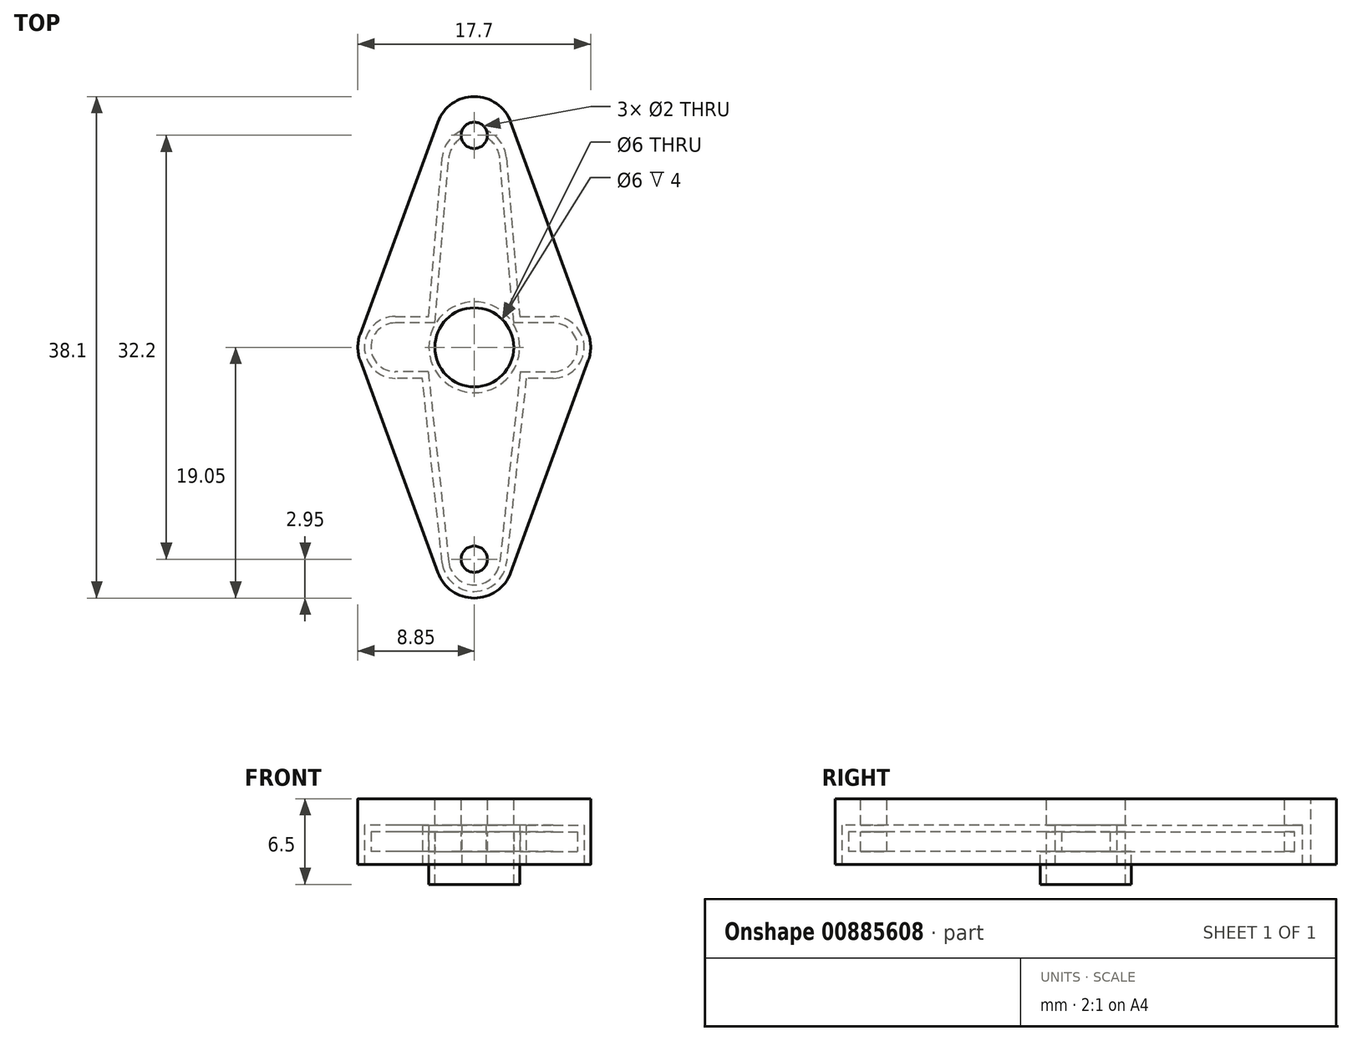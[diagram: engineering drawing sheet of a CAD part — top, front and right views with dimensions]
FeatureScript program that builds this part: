
annotation { "Feature Type Name" : "Feature", "Feature Type Description" : "" }
export const myFeature = defineFeature(function(context is Context, id is Id, definition is map)
    precondition{}
    {
        {
            var Q0;
            Q0=qCreatedBy(makeId("Top.planeOp"),FACE);
            var sketch = newSketch(context, id + "F0", { "sketchPlane" : qUnion([Q0])});
            skLineSegment(sketch, "E0.bottom", {"start": v(3.5, 1.85) * mm, "end": v(-3.5, 1.85) * mm});
            skLineSegment(sketch, "E0.top", {"start": v(3.5, -1.85) * mm, "end": v(-3.5, -1.85) * mm});
            skLineSegment(sketch, "E0.left", {"start": v(3.5, 1.85) * mm, "end": v(3.5, -1.85) * mm});
            skLineSegment(sketch, "E0.right", {"start": v(-3.5, 1.85) * mm, "end": v(-3.5, -1.85) * mm});
            skPoint(sketch, "E0.middle", {"position": v(0, 0) * mm});
            skLineSegment(sketch, "E1", {"start": v(0, 0) * mm, "end": v(0, 14.2) * mm});
            skCircle(sketch, "E2", {"center": v(0, 14.2) * mm, "radius": 1.95 * mm});
            skLineSegment(sketch, "E3", {"start": v(0, 0) * mm, "end": v(0, -16.1) * mm});
            skCircle(sketch, "E4", {"center": v(0, -16.1) * mm, "radius": 1.95 * mm});
            skLineSegment(sketch, "E5", {"start": v(0, 0) * mm, "end": v(-6, 0) * mm});
            skLineSegment(sketch, "E6", {"start": v(0, 0) * mm, "end": v(6, 0) * mm});
            skCircle(sketch, "E7", {"center": v(6, 0) * mm, "radius": 1.85 * mm});
            skCircle(sketch, "E8", {"center": v(-6, 0) * mm, "radius": 1.85 * mm});
            skLineSegment(sketch, "E9", {"start": v(3.5, 1.85) * mm, "end": v(6, 1.85) * mm});
            skLineSegment(sketch, "E10", {"start": v(3.5, -1.85) * mm, "end": v(6, -1.85) * mm});
            skLineSegment(sketch, "E11", {"start": v(-3.5, 1.85) * mm, "end": v(-6, 1.85) * mm});
            skLineSegment(sketch, "E12", {"start": v(-3.5, -1.85) * mm, "end": v(-6, -1.85) * mm});
            skLineSegment(sketch, "E13", {"start": v(3.5, -1.85) * mm, "end": v(1.94, -16.3) * mm});
            skLineSegment(sketch, "E14", {"start": v(-3.5, -1.85) * mm, "end": v(-1.94, -16.3) * mm});
            skLineSegment(sketch, "E15", {"start": v(-3, 1.85) * mm, "end": v(-1.94, 14.36) * mm});
            skLineSegment(sketch, "E16", {"start": v(3, 1.85) * mm, "end": v(1.94, 14.36) * mm});
            skSolve(sketch);
        }
        {
            var Q0;
            {var subQ0=sQuery(id+"F0.wireOp",EDGE,"E2");var subQ1=makeQuery(id+"F0.imprint","INTERSECT",VERTEX,{"derivedFrom":[subQ0,sQuery(id+"F0.wireOp",EDGE,"E5d6Bwbx-nQxb-vEjo-hPbS-5jYDuID1mhCR")]});Q0=makeQuery(id+"F0.imprint","IMPRINT",FACE,{"disambiguationData":[TD([[makeQuery(id+"F0.imprint","IMPRINT",EDGE,{"disambiguationData":[TD([[subQ1,-1.0]])],"derivedFrom":subQ0}),1.0]])]});}
            var Q1;
            {var subQ0=sQuery(id+"F0.wireOp",EDGE,"E5d6Bwbx-nQxb-vEjo-hPbS-5jYDuID1mhCR");Q1=makeQuery(id+"F0.imprint","IMPRINT",FACE,{"disambiguationData":[TD([[makeQuery(id+"F0.imprint","IMPRINT",EDGE,{"derivedFrom":subQ0}),1.0]])]});}
            var Q2;
            {var subQ0=sQuery(id+"F0.wireOp",EDGE,"Ki0dr052-tBK0-U8Og-YfLE-ReEXXek7wxif");Q2=makeQuery(id+"F0.imprint","IMPRINT",FACE,{"disambiguationData":[TD([[makeQuery(id+"F0.imprint","IMPRINT",EDGE,{"derivedFrom":subQ0}),-1.0]])]});}
            var Q3;
            {var subQ1=sQuery(id+"F0.wireOp",EDGE,"E0.bottom");var subQ3=sQuery(id+"F0.wireOp",EDGE,"E1");var subQ4=makeQuery(id+"F0.imprint","INTERSECT",VERTEX,{"derivedFrom":[subQ1,subQ3]});Q3=makeQuery(id+"F0.imprint","IMPRINT",FACE,{"disambiguationData":[TD([[makeQuery(id+"F0.imprint","IMPRINT",EDGE,{"disambiguationData":[TD([[subQ4,-1.0]])],"derivedFrom":subQ1}),1.0]])]});}
            var Q4;
            {var subQ1=sQuery(id+"F0.wireOp",EDGE,"E0.bottom");var subQ3=sQuery(id+"F0.wireOp",EDGE,"E1");var subQ4=makeQuery(id+"F0.imprint","INTERSECT",VERTEX,{"derivedFrom":[subQ1,subQ3]});Q4=makeQuery(id+"F0.imprint","IMPRINT",FACE,{"disambiguationData":[TD([[makeQuery(id+"F0.imprint","IMPRINT",EDGE,{"disambiguationData":[TD([[subQ4,1.0]])],"derivedFrom":subQ1}),1.0]])]});}
            var Q5;
            {var subQ1=sQuery(id+"F0.wireOp",EDGE,"E0.top");var subQ3=sQuery(id+"F0.wireOp",EDGE,"E3");var subQ4=makeQuery(id+"F0.imprint","INTERSECT",VERTEX,{"derivedFrom":[subQ1,subQ3]});Q5=makeQuery(id+"F0.imprint","IMPRINT",FACE,{"disambiguationData":[TD([[makeQuery(id+"F0.imprint","IMPRINT",EDGE,{"disambiguationData":[TD([[subQ4,1.0]])],"derivedFrom":subQ1}),-1.0]])]});}
            var Q6;
            {var subQ1=sQuery(id+"F0.wireOp",EDGE,"E0.top");var subQ3=sQuery(id+"F0.wireOp",EDGE,"E3");var subQ4=makeQuery(id+"F0.imprint","INTERSECT",VERTEX,{"derivedFrom":[subQ1,subQ3]});Q6=makeQuery(id+"F0.imprint","IMPRINT",FACE,{"disambiguationData":[TD([[makeQuery(id+"F0.imprint","IMPRINT",EDGE,{"disambiguationData":[TD([[subQ4,-1.0]])],"derivedFrom":subQ1}),-1.0]])]});}
            var Q7;
            {var subQ0=sQuery(id+"F0.wireOp",EDGE,"E12");Q7=makeQuery(id+"F0.imprint","IMPRINT",FACE,{"disambiguationData":[TD([[makeQuery(id+"F0.imprint","IMPRINT",EDGE,{"derivedFrom":subQ0}),-1.0]])]});}
            var Q8;
            {var subQ0=sQuery(id+"F0.wireOp",EDGE,"E11");Q8=makeQuery(id+"F0.imprint","IMPRINT",FACE,{"disambiguationData":[TD([[makeQuery(id+"F0.imprint","IMPRINT",EDGE,{"derivedFrom":subQ0}),1.0]])]});}
            var Q9;
            {var subQ0=sQuery(id+"F0.wireOp",EDGE,"E8");var subQ1=makeQuery(id+"F0.imprint","INTERSECT",VERTEX,{"derivedFrom":[subQ0,sQuery(id+"F0.wireOp",EDGE,"E11")]});Q9=makeQuery(id+"F0.imprint","IMPRINT",FACE,{"disambiguationData":[TD([[makeQuery(id+"F0.imprint","IMPRINT",EDGE,{"disambiguationData":[TD([[subQ1,1.0]])],"derivedFrom":subQ0}),1.0]])]});}
            var Q10;
            {var subQ0=sQuery(id+"F0.wireOp",EDGE,"E7");var subQ1=makeQuery(id+"F0.imprint","INTERSECT",VERTEX,{"derivedFrom":[subQ0,sQuery(id+"F0.wireOp",EDGE,"E9")]});Q10=makeQuery(id+"F0.imprint","IMPRINT",FACE,{"disambiguationData":[TD([[makeQuery(id+"F0.imprint","IMPRINT",EDGE,{"disambiguationData":[TD([[subQ1,-1.0]])],"derivedFrom":subQ0}),1.0]])]});}
            var Q11;
            {var subQ0=sQuery(id+"F0.wireOp",EDGE,"E9");Q11=makeQuery(id+"F0.imprint","IMPRINT",FACE,{"disambiguationData":[TD([[makeQuery(id+"F0.imprint","IMPRINT",EDGE,{"derivedFrom":subQ0}),-1.0]])]});}
            var Q12;
            {var subQ0=sQuery(id+"F0.wireOp",EDGE,"E10");Q12=makeQuery(id+"F0.imprint","IMPRINT",FACE,{"disambiguationData":[TD([[makeQuery(id+"F0.imprint","IMPRINT",EDGE,{"derivedFrom":subQ0}),1.0]])]});}
            var Q13;
            {var subQ0=sQuery(id+"F0.wireOp",EDGE,"E13");Q13=makeQuery(id+"F0.imprint","IMPRINT",FACE,{"disambiguationData":[TD([[makeQuery(id+"F0.imprint","IMPRINT",EDGE,{"derivedFrom":subQ0}),-1.0]])]});}
            var Q14;
            {var subQ0=sQuery(id+"F0.wireOp",EDGE,"E14");Q14=makeQuery(id+"F0.imprint","IMPRINT",FACE,{"disambiguationData":[TD([[makeQuery(id+"F0.imprint","IMPRINT",EDGE,{"derivedFrom":subQ0}),1.0]])]});}
            var Q15;
            {var subQ0=sQuery(id+"F0.wireOp",EDGE,"E4");var subQ1=makeQuery(id+"F0.imprint","INTERSECT",VERTEX,{"derivedFrom":[subQ0,sQuery(id+"F0.wireOp",EDGE,"E14")]});Q15=makeQuery(id+"F0.imprint","IMPRINT",FACE,{"disambiguationData":[TD([[makeQuery(id+"F0.imprint","IMPRINT",EDGE,{"disambiguationData":[TD([[subQ1,1.0]])],"derivedFrom":subQ0}),1.0]])]});}
            var Q16;
            {var subQ0=sQuery(id+"F0.wireOp",EDGE,"E16");Q16=makeQuery(id+"F0.imprint","IMPRINT",FACE,{"disambiguationData":[TD([[makeQuery(id+"F0.imprint","IMPRINT",EDGE,{"derivedFrom":subQ0}),1.0]])]});}
            var Q17;
            {var subQ0=sQuery(id+"F0.wireOp",EDGE,"E15");Q17=makeQuery(id+"F0.imprint","IMPRINT",FACE,{"disambiguationData":[TD([[makeQuery(id+"F0.imprint","IMPRINT",EDGE,{"derivedFrom":subQ0}),-1.0]])]});}
            extrude(context, id + "F1", {"entities" : qUnion([Q0, Q1, Q2, Q3, Q4, Q5, Q6, Q7, Q8, Q9, Q10, Q11, Q12, Q13, Q14, Q15, Q16, Q17]), "depth" : 1.5 * mm, "offsetDistance" : 25 * mm});
        }
        {
            var Q0;
            Q0=makeQuery(id+"F1.opExtrude","CAP_FACE",FACE,{"disambiguationData":[OSD([sQuery(id+"F0.wireOp",EDGE,"E2"),sQuery(id+"F0.wireOp",EDGE,"E4"),sQuery(id+"F0.wireOp",EDGE,"E7"),sQuery(id+"F0.wireOp",EDGE,"E8"),sQuery(id+"F0.wireOp",EDGE,"E9"),sQuery(id+"F0.wireOp",EDGE,"E10"),sQuery(id+"F0.wireOp",EDGE,"E11"),sQuery(id+"F0.wireOp",EDGE,"E12"),sQuery(id+"F0.wireOp",EDGE,"E5d6Bwbx-nQxb-vEjo-hPbS-5jYDuID1mhCR"),sQuery(id+"F0.wireOp",EDGE,"Ki0dr052-tBK0-U8Og-YfLE-ReEXXek7wxif"),sQuery(id+"F0.wireOp",EDGE,"E13"),sQuery(id+"F0.wireOp",EDGE,"E14")])],"isStart":true});
            var sketch = newSketch(context, id + "F2", { "sketchPlane" : qUnion([Q0])});
            skCircle(sketch, "E17", {"center": v(0, 0) * mm, "radius": 3.45 * mm});
            skSolve(sketch);
        }
        {
            var Q0;
            Q0=makeQuery(id+"F2.imprint","IMPRINT",FACE,{"disambiguationData":[TD([[makeQuery(id+"F2.imprint","IMPRINT",EDGE,{"derivedFrom":sQuery(id+"F2.wireOp",EDGE,"E17")}),1.0]])]});
            extrude(context, id + "F3", {"entities" : qUnion([Q0]), "operationType" : NewBodyOperationType.ADD, "depth" : 2.5 * mm, "offsetDistance" : 25 * mm});
        }
        {
            var Q0;
            Q0=makeQuery(id+"F1.opExtrude","CAP_FACE",FACE,{"disambiguationData":[OSD([sQuery(id+"F0.wireOp",EDGE,"E2"),sQuery(id+"F0.wireOp",EDGE,"E4"),sQuery(id+"F0.wireOp",EDGE,"E7"),sQuery(id+"F0.wireOp",EDGE,"E8"),sQuery(id+"F0.wireOp",EDGE,"E9"),sQuery(id+"F0.wireOp",EDGE,"E10"),sQuery(id+"F0.wireOp",EDGE,"E11"),sQuery(id+"F0.wireOp",EDGE,"E12"),sQuery(id+"F0.wireOp",EDGE,"E5d6Bwbx-nQxb-vEjo-hPbS-5jYDuID1mhCR"),sQuery(id+"F0.wireOp",EDGE,"Ki0dr052-tBK0-U8Og-YfLE-ReEXXek7wxif"),sQuery(id+"F0.wireOp",EDGE,"E13"),sQuery(id+"F0.wireOp",EDGE,"E14")])],"isStart":false});
            var sketch = newSketch(context, id + "F4", { "sketchPlane" : qUnion([Q0])});
            skCircle(sketch, "E18", {"center": v(0, -16.1) * mm, "radius": 2.95 * mm});
            skCircle(sketch, "E19", {"center": v(-6, 0) * mm, "radius": 2.85 * mm});
            skLineSegment(sketch, "E20", {"start": v(-2.77, -17.11) * mm, "end": v(-8.68, -0.98) * mm});
            skCircle(sketch, "E21.MirrorC", {"center": v(0, 16.1) * mm, "radius": 2.95 * mm});
            skLineSegment(sketch, "E22.MirrorCS", {"start": v(-2.77, 17.11) * mm, "end": v(-8.68, 0.98) * mm});
            skCircle(sketch, "E23.MirrorC", {"center": v(6, 0) * mm, "radius": 2.85 * mm});
            skLineSegment(sketch, "E24.MirrorCS", {"start": v(2.77, -17.11) * mm, "end": v(8.68, -0.98) * mm});
            skLineSegment(sketch, "E25.MirrorCS", {"start": v(2.77, 17.11) * mm, "end": v(8.68, 0.98) * mm});
            skSolve(sketch);
        }
        {
            var Q0;
            Q0 = qSketchRegion(id + "F4", true);
            extrude(context, id + "F5", {"entities" : qUnion([Q0]), "depth" : 3 * mm, "offsetDistance" : 25 * mm, "symmetric" : true});
        }
        {
            var Q0;
            Q0=makeQuery(id+"F1.opExtrude","SWEPT_BODY",BODY,{"disambiguationData":[OSD([sQuery(id+"F0.wireOp",EDGE,"E2"),sQuery(id+"F0.wireOp",EDGE,"E4"),sQuery(id+"F0.wireOp",EDGE,"E7"),sQuery(id+"F0.wireOp",EDGE,"E8"),sQuery(id+"F0.wireOp",EDGE,"E9"),sQuery(id+"F0.wireOp",EDGE,"E10"),sQuery(id+"F0.wireOp",EDGE,"E11"),sQuery(id+"F0.wireOp",EDGE,"E12"),sQuery(id+"F0.wireOp",EDGE,"E5d6Bwbx-nQxb-vEjo-hPbS-5jYDuID1mhCR"),sQuery(id+"F0.wireOp",EDGE,"Ki0dr052-tBK0-U8Og-YfLE-ReEXXek7wxif"),sQuery(id+"F0.wireOp",EDGE,"E13"),sQuery(id+"F0.wireOp",EDGE,"E14")])]});
            var Q1;
            Q1=makeQuery(id+"F5.opExtrude","SWEPT_BODY",BODY,{"disambiguationData":[OSD([sQuery(id+"F4.wireOp",EDGE,"E20"),sQuery(id+"F4.wireOp",EDGE,"E19"),sQuery(id+"F4.wireOp",EDGE,"E22.MirrorCS"),sQuery(id+"F4.wireOp",EDGE,"E23.MirrorC"),sQuery(id+"F4.wireOp",EDGE,"E24.MirrorCS"),sQuery(id+"F4.wireOp",EDGE,"E21.MirrorC"),sQuery(id+"F4.wireOp",EDGE,"E25.MirrorCS"),sQuery(id+"F4.wireOp",EDGE,"E18")])]});
            booleanBodies(context, id + "F6", {"operationType" : BooleanOperationType.SUBTRACTION, "tools" : qUnion([Q0]), "targets" : qUnion([Q1]), "offset" : true, "offsetAll" : true, "offsetDistance" : .5 * mm, "keepTools" : true});
        }
        {
            var Q0;
            Q0=makeQuery(id+"F5.opExtrude","CAP_FACE",FACE,{"disambiguationData":[OSD([sQuery(id+"F4.wireOp",EDGE,"E20"),sQuery(id+"F4.wireOp",EDGE,"E19"),sQuery(id+"F4.wireOp",EDGE,"E22.MirrorCS"),sQuery(id+"F4.wireOp",EDGE,"E23.MirrorC"),sQuery(id+"F4.wireOp",EDGE,"E24.MirrorCS"),sQuery(id+"F4.wireOp",EDGE,"E21.MirrorC"),sQuery(id+"F4.wireOp",EDGE,"E25.MirrorCS"),sQuery(id+"F4.wireOp",EDGE,"E18")])],"isStart":false});
            var sketch = newSketch(context, id + "F7", { "sketchPlane" : qUnion([Q0])});
            skCircle(sketch, "E26", {"center": v(0, 0) * mm, "radius": 3 * mm});
            skSolve(sketch);
        }
        {
            var Q0;
            Q0 = qSketchRegion(id + "F7", true);
            extrude(context, id + "F8", {"entities" : qUnion([Q0]), "operationType" : NewBodyOperationType.REMOVE, "oppositeDirection" : true, "depth" : 10 * mm, "offsetDistance" : 25 * mm});
        }
        {
            var Q0;
            Q0=makeQuery(id+"F5.opExtrude","CAP_FACE",FACE,{"disambiguationData":[OSD([sQuery(id+"F4.wireOp",EDGE,"E20"),sQuery(id+"F4.wireOp",EDGE,"E19"),sQuery(id+"F4.wireOp",EDGE,"E22.MirrorCS"),sQuery(id+"F4.wireOp",EDGE,"E23.MirrorC"),sQuery(id+"F4.wireOp",EDGE,"E24.MirrorCS"),sQuery(id+"F4.wireOp",EDGE,"E21.MirrorC"),sQuery(id+"F4.wireOp",EDGE,"E25.MirrorCS"),sQuery(id+"F4.wireOp",EDGE,"E18")])],"isStart":false});
            extrude(context, id + "F9", {"entities" : qUnion([Q0]), "operationType" : NewBodyOperationType.ADD, "depth" : 1 * mm, "offsetDistance" : 25 * mm});
        }
        {
            var Q0;
            Q0=makeQuery(id+"F5.opExtrude","CAP_FACE",FACE,{"disambiguationData":[OSD([sQuery(id+"F4.wireOp",EDGE,"E20"),sQuery(id+"F4.wireOp",EDGE,"E19"),sQuery(id+"F4.wireOp",EDGE,"E22.MirrorCS"),sQuery(id+"F4.wireOp",EDGE,"E23.MirrorC"),sQuery(id+"F4.wireOp",EDGE,"E24.MirrorCS"),sQuery(id+"F4.wireOp",EDGE,"E21.MirrorC"),sQuery(id+"F4.wireOp",EDGE,"E25.MirrorCS"),sQuery(id+"F4.wireOp",EDGE,"E18")])],"isStart":true});
            extrude(context, id + "F10", {"entities" : qUnion([Q0]), "operationType" : NewBodyOperationType.ADD, "depth" : 1 * mm, "offsetDistance" : 25 * mm});
        }
        {
            var Q0;
            Q0=makeQuery(id+"F9.opExtrude","CAP_FACE",FACE,{"disambiguationData":[OSD([sQuery(id+"F4.wireOp",EDGE,"E20"),sQuery(id+"F4.wireOp",EDGE,"E19"),sQuery(id+"F4.wireOp",EDGE,"E22.MirrorCS"),sQuery(id+"F4.wireOp",EDGE,"E23.MirrorC"),sQuery(id+"F4.wireOp",EDGE,"E24.MirrorCS"),sQuery(id+"F4.wireOp",EDGE,"E21.MirrorC"),sQuery(id+"F4.wireOp",EDGE,"E25.MirrorCS"),sQuery(id+"F4.wireOp",EDGE,"E18")])],"isStart":false});
            var sketch = newSketch(context, id + "F11", { "sketchPlane" : qUnion([Q0])});
            skCircle(sketch, "E27", {"center": v(0, -16.1) * mm, "radius": 1 * mm});
            skCircle(sketch, "E28.MirrorC", {"center": v(0, 16.1) * mm, "radius": 1 * mm});
            skSolve(sketch);
        }
        {
            var Q0;
            Q0 = qSketchRegion(id + "F11", true);
            extrude(context, id + "F12", {"entities" : qUnion([Q0]), "operationType" : NewBodyOperationType.REMOVE, "oppositeDirection" : true, "depth" : 10 * mm, "offsetDistance" : 25 * mm});
        }
    });
